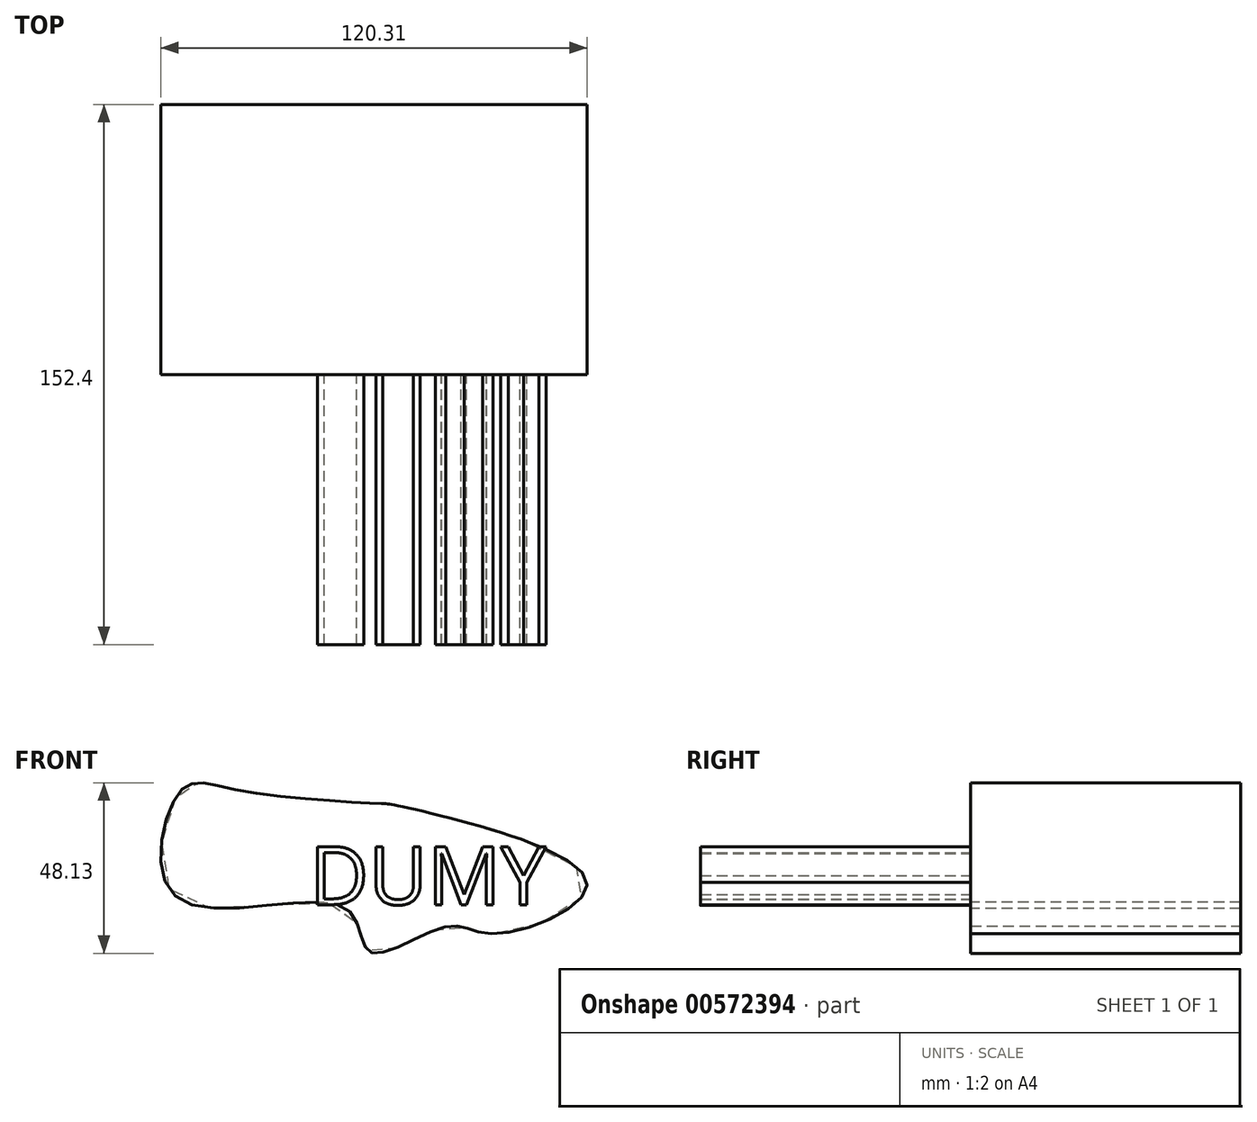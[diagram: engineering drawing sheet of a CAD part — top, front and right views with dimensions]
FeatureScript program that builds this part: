
annotation { "Feature Type Name" : "Feature", "Feature Type Description" : "" }
export const myFeature = defineFeature(function(context is Context, id is Id, definition is map)
    precondition{}
    {
        {
            var Q0;
            Q0=qCreatedBy(makeId("Front.planeOp"),FACE);
            var sketch = newSketch(context, id + "F0", { "sketchPlane" : qUnion([Q0])});
            skFitSpline(sketch, "E0", {"points": [v(-11.24, 21.58) * mm, v(-52, 25.4) * mm, v(-68.06, 25) * mm, v(-69.07, -4.92) * mm, v(-21.48, -7.93) * mm, v(-14.46, -20.38) * mm, v(7.03, -13.15) * mm, v(21.08, -15.16) * mm, v(46.58, -0.1) * mm, v(-6.83, 20.98) * mm, v(-11.24, 21.58) * mm]});
            skSolve(sketch);
        }
        {
            var Q0;
            Q0 = qSketchRegion(id + "F0", true);
            extrude(context, id + "F1", {"entities" : qUnion([Q0]), "depth" : 76.2 * mm, "offsetDistance" : 25.4 * mm});
        }
        {
            var Q0;
            Q0=makeQuery(id+"F1.opExtrude","CAP_FACE",FACE,{"disambiguationData":[OSD([sQuery(id+"F0.wireOp",EDGE,"E0")])],"isStart":false});
            var sketch = newSketch(context, id + "F2", { "sketchPlane" : qUnion([Q0])});
            skText(sketch, "E1", { "text": "DUMY", "fontName": "OpenSans-Regular.ttf"});
            const initialGuessF2  = {"E1": [-0.03158, -0.00696, 1, 0, 0.01647]};
            skSetInitialGuess(sketch, initialGuessF2);
            skSolve(sketch);
        }
        {
            var Q0;
            Q0 = qSketchRegion(id + "F2", true);
            extrude(context, id + "F3", {"entities" : qUnion([Q0]), "operationType" : NewBodyOperationType.ADD, "depth" : 76.2 * mm, "offsetDistance" : 25.4 * mm});
        }
    });
